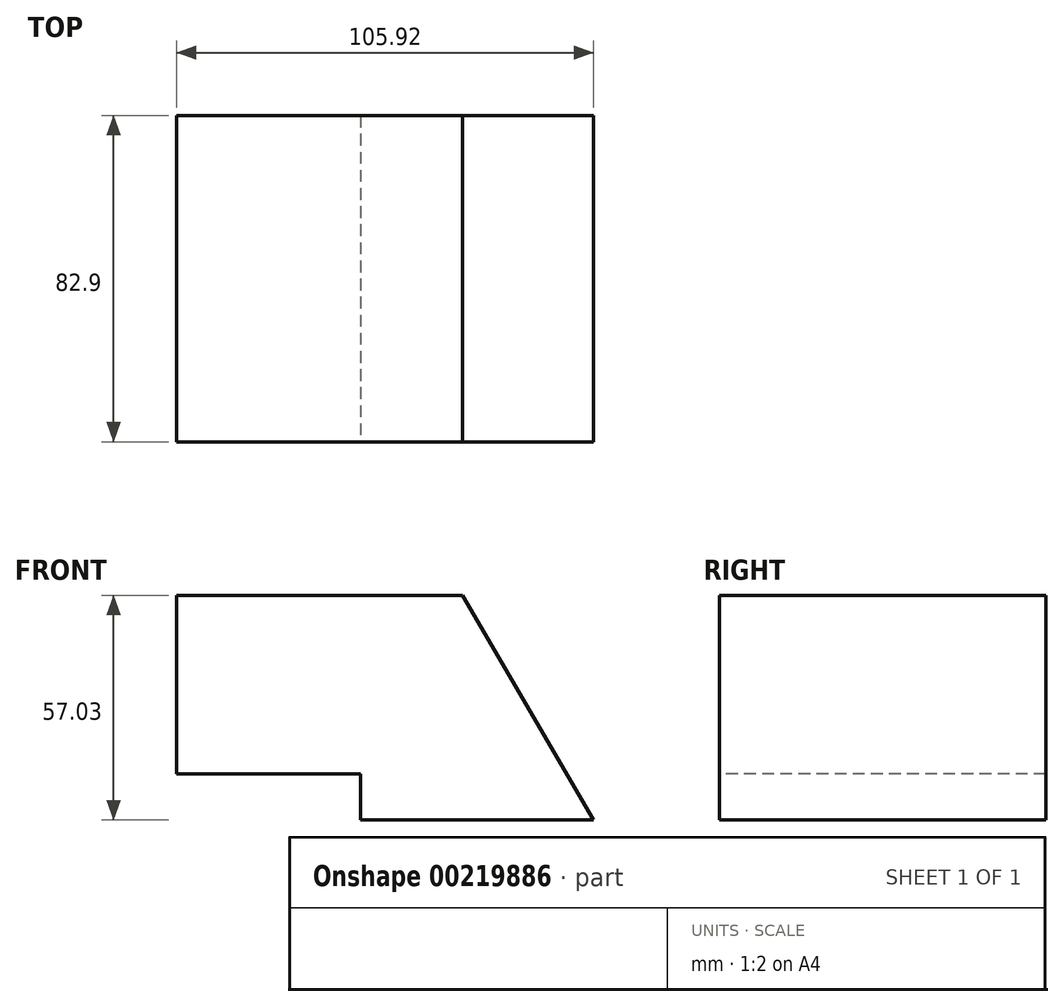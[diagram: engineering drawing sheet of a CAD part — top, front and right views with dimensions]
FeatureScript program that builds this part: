
annotation { "Feature Type Name" : "Feature", "Feature Type Description" : "" }
export const myFeature = defineFeature(function(context is Context, id is Id, definition is map)
    precondition{}
    {
        {
            var Q0;
            Q0=qCreatedBy(makeId("Right.planeOp"),FACE);
            var sketch = newSketch(context, id + "F0", { "sketchPlane" : qUnion([Q0])});
            skLineSegment(sketch, "E0.bottom", {"start": v(-38.33, 27.6) * mm, "end": v(44.57, 27.6) * mm});
            skLineSegment(sketch, "E0.top", {"start": v(-38.33, -29.44) * mm, "end": v(44.57, -29.44) * mm});
            skLineSegment(sketch, "E0.left", {"start": v(-38.33, 27.6) * mm, "end": v(-38.33, -29.44) * mm});
            skLineSegment(sketch, "E0.right", {"start": v(44.57, 27.6) * mm, "end": v(44.57, -29.44) * mm});
            skSolve(sketch);
        }
        {
            var Q0;
            Q0=makeQuery(id+"F0.imprint","IMPRINT",FACE,{"disambiguationData":[TD([[makeQuery(id+"F0.imprint","IMPRINT",EDGE,{"derivedFrom":sQuery(id+"F0.wireOp",EDGE,"E0.bottom")}),-1.0]])]});
            extrude(context, id + "F1", {"entities" : qUnion([Q0]), "oppositeDirection" : true, "depth" : 105.92 * mm});
        }
        {
            var Q0;
            Q0=makeQuery(id+"F1.opExtrude","SWEPT_FACE",FACE,{"disambiguationData":[OSD([sQuery(id+"F0.wireOp",EDGE,"E0.left")])]});
            var sketch = newSketch(context, id + "F2", { "sketchPlane" : qUnion([Q0])});
            skLineSegment(sketch, "E1.0", {"start": v(-105.92, 27.6) * mm, "end": v(0, 27.6) * mm});
            skLineSegment(sketch, "E2.0", {"start": v(0, 27.6) * mm, "end": v(0, -29.44) * mm});
            skLineSegment(sketch, "E3", {"start": v(-33.2, 27.6) * mm, "end": v(0, 27.6) * mm});
            skLineSegment(sketch, "E4", {"start": v(0, -29.44) * mm, "end": v(-33.2, 27.6) * mm});
            skSolve(sketch);
        }
        {
            var Q0;
            Q0=makeQuery(id+"F2.imprint","IMPRINT",FACE,{"disambiguationData":[TD([[makeQuery(id+"F2.imprint","IMPRINT",EDGE,{"derivedFrom":sQuery(id+"F2.wireOp",EDGE,"E2.0")}),-1.0]])]});
            extrude(context, id + "F3", {"entities" : qUnion([Q0]), "operationType" : NewBodyOperationType.REMOVE, "endBound" : BoundingType.THROUGH_ALL, "oppositeDirection" : true, "depth" : 25.4 * mm});
        }
        {
            var Q0;
            Q0=makeQuery(id+"F1.opExtrude","SWEPT_FACE",FACE,{"disambiguationData":[OSD([sQuery(id+"F0.wireOp",EDGE,"E0.left")])]});
            var sketch = newSketch(context, id + "F4", { "sketchPlane" : qUnion([Q0])});
            skLineSegment(sketch, "E5.0", {"start": v(-105.92, 27.6) * mm, "end": v(-33.2, 27.6) * mm});
            skLineSegment(sketch, "E6.0", {"start": v(0, -29.44) * mm, "end": v(-33.2, 27.6) * mm});
            skLineSegment(sketch, "E7.0", {"start": v(-105.92, 27.6) * mm, "end": v(-105.92, -29.44) * mm});
            skLineSegment(sketch, "E8.0", {"start": v(-105.92, -29.44) * mm, "end": v(0, -29.44) * mm});
            skLineSegment(sketch, "E9", {"start": v(-105.92, -17.72) * mm, "end": v(-59.19, -17.72) * mm});
            skLineSegment(sketch, "E10", {"start": v(-59.19, -17.72) * mm, "end": v(-59.19, -29.44) * mm});
            skSolve(sketch);
        }
        {
            var Q0;
            {var subQ3=sQuery(id+"F4.wireOp",EDGE,"E9");Q0=makeQuery(id+"F4.imprint","IMPRINT",FACE,{"disambiguationData":[TD([[makeQuery(id+"F4.imprint","IMPRINT",EDGE,{"derivedFrom":subQ3}),-1.0]])]});}
            extrude(context, id + "F5", {"entities" : qUnion([Q0]), "operationType" : NewBodyOperationType.REMOVE, "endBound" : BoundingType.THROUGH_ALL, "oppositeDirection" : true, "depth" : 25.4 * mm});
        }
    });
